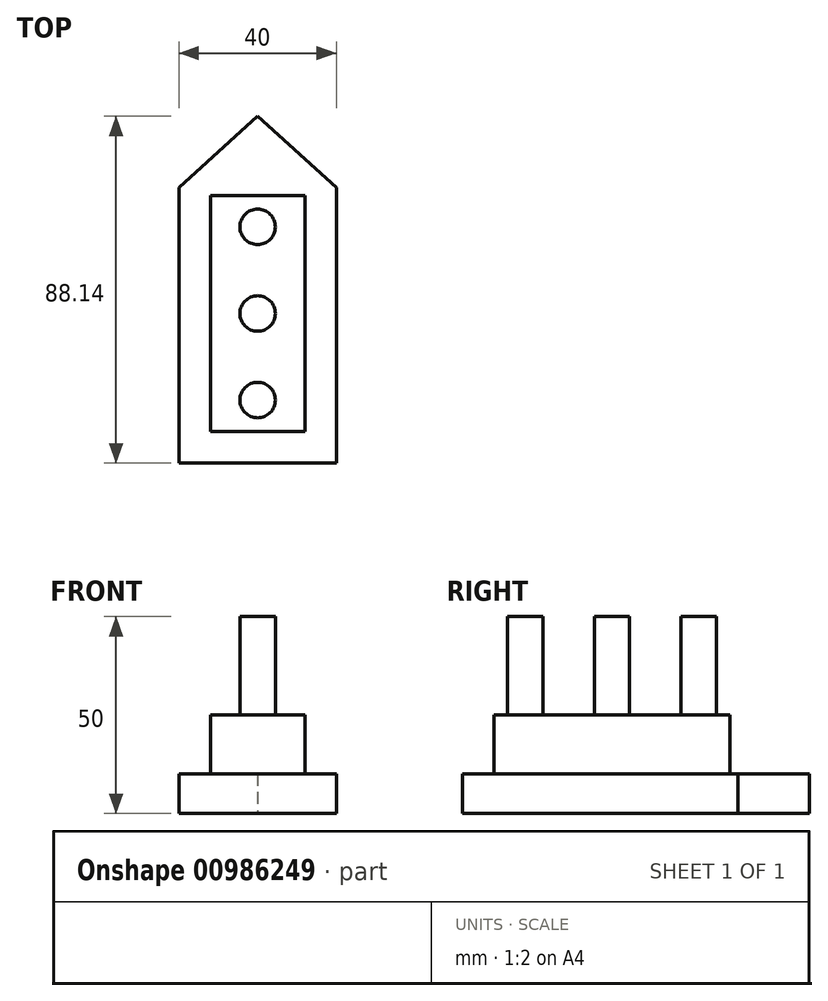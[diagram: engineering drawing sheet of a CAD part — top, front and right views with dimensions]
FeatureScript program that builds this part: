
annotation { "Feature Type Name" : "Feature", "Feature Type Description" : "" }
export const myFeature = defineFeature(function(context is Context, id is Id, definition is map)
    precondition{}
    {
        {
            var Q0;
            Q0=qCreatedBy(makeId("Top.planeOp"),FACE);
            var sketch = newSketch(context, id + "F0", { "sketchPlane" : qUnion([Q0])});
            skLineSegment(sketch, "E0", {"start": v(-20, 35.52) * mm, "end": v(-20, -34.48) * mm});
            skLineSegment(sketch, "E1", {"start": v(-20, -34.48) * mm, "end": v(20, -34.48) * mm});
            skLineSegment(sketch, "E2", {"start": v(20, -34.48) * mm, "end": v(20, 35.52) * mm});
            skLineSegment(sketch, "E3", {"start": v(20, 35.52) * mm, "end": v(0, 53.66) * mm});
            skLineSegment(sketch, "E4", {"start": v(0, 53.66) * mm, "end": v(-20, 35.52) * mm});
            skSolve(sketch);
        }
        {
            var Q0;
            Q0 = qSketchRegion(id + "F0", true);
            extrude(context, id + "F1", {"entities" : qUnion([Q0]), "depth" : 10 * mm, "offsetDistance" : 25 * mm});
        }
        {
            var Q0;
            Q0=qCreatedBy(makeId("Top.planeOp"),FACE);
            var sketch = newSketch(context, id + "F2", { "sketchPlane" : qUnion([Q0])});
            skLineSegment(sketch, "E5.bottom", {"start": v(-12, 33.52) * mm, "end": v(12, 33.52) * mm});
            skLineSegment(sketch, "E5.top", {"start": v(-12, -26.48) * mm, "end": v(12, -26.48) * mm});
            skLineSegment(sketch, "E5.left", {"start": v(-12, 33.52) * mm, "end": v(-12, -26.48) * mm});
            skLineSegment(sketch, "E5.right", {"start": v(12, 33.52) * mm, "end": v(12, -26.48) * mm});
            skSolve(sketch);
        }
        {
            var Q0;
            Q0 = qSketchRegion(id + "F2", true);
            extrude(context, id + "F3", {"entities" : qUnion([Q0]), "operationType" : NewBodyOperationType.ADD, "depth" : 25 * mm, "offsetDistance" : 25 * mm});
        }
        {
            var Q0;
            Q0=makeQuery(id+"F3.opExtrude","CAP_FACE",FACE,{"disambiguationData":[OSD([sQuery(id+"F2.wireOp",EDGE,"E5.bottom"),sQuery(id+"F2.wireOp",EDGE,"E5.top"),sQuery(id+"F2.wireOp",EDGE,"E5.left"),sQuery(id+"F2.wireOp",EDGE,"E5.right")])],"isStart":false});
            var sketch = newSketch(context, id + "F4", { "sketchPlane" : qUnion([Q0])});
            skCircle(sketch, "E6", {"center": v(0, 25.52) * mm, "radius": 4.5 * mm});
            skCircle(sketch, "E7", {"center": v(0, 3.52) * mm, "radius": 4.5 * mm});
            skCircle(sketch, "E8", {"center": v(0, -18.48) * mm, "radius": 4.5 * mm});
            skSolve(sketch);
        }
        {
            var Q0;
            Q0 = qSketchRegion(id + "F4", true);
            extrude(context, id + "F5", {"entities" : qUnion([Q0]), "operationType" : NewBodyOperationType.ADD, "depth" : 25 * mm, "offsetDistance" : 25 * mm});
        }
    });
